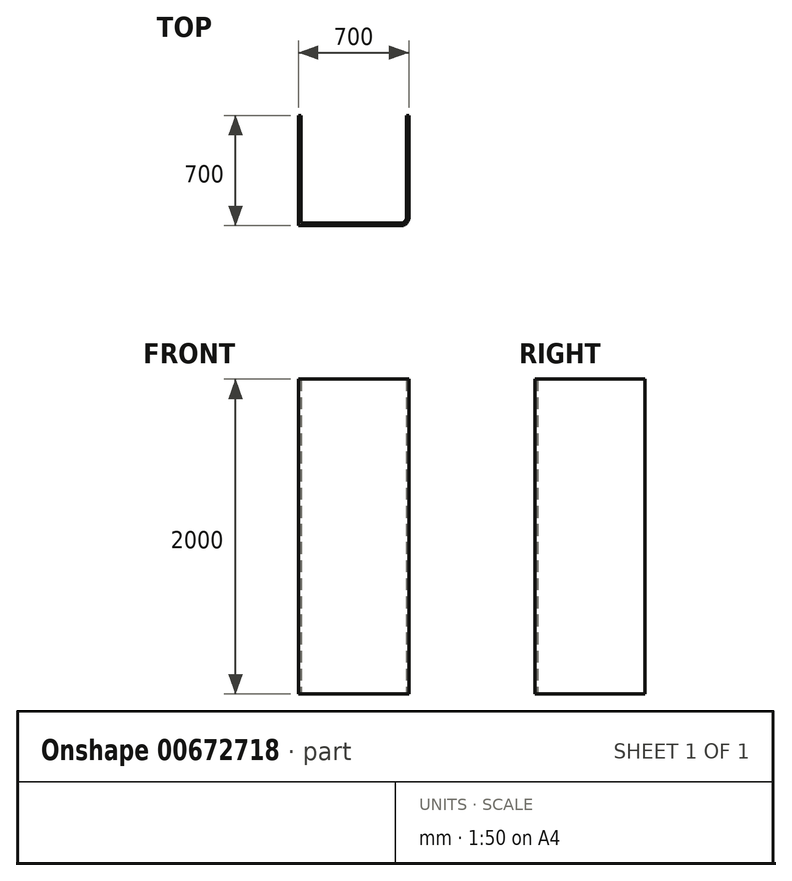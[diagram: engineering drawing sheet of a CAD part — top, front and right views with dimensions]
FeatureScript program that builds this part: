
annotation { "Feature Type Name" : "Feature", "Feature Type Description" : "" }
export const myFeature = defineFeature(function(context is Context, id is Id, definition is map)
    precondition{}
    {
        {
            var Q0;
            Q0=qCreatedBy(makeId("Top.planeOp"),FACE);
            var sketch = newSketch(context, id + "F0", { "sketchPlane" : qUnion([Q0])});
            skLineSegment(sketch, "E0.bottom", {"start": v(0, 0) * mm, "end": v(-700, 0) * mm});
            skLineSegment(sketch, "E0.top", {"start": v(0, -700) * mm, "end": v(-700, -700) * mm});
            skLineSegment(sketch, "E0.left", {"start": v(0, 0) * mm, "end": v(0, -700) * mm});
            skLineSegment(sketch, "E0.right", {"start": v(-700, 0) * mm, "end": v(-700, -700) * mm});
            skSolve(sketch);
        }
        {
            var Q0;
            Q0=makeQuery(id+"F0.imprint","IMPRINT",FACE,{"disambiguationData":[TD([[makeQuery(id+"F0.imprint","IMPRINT",EDGE,{"derivedFrom":sQuery(id+"F0.wireOp",EDGE,"Y66rWitT-qBWe-ztKi-yuPp-pPcdfemAuZkT.bottom")}),-1.0]])]});
            var Q1;
            Q1=makeQuery(id+"F0.imprint","IMPRINT",FACE,{"disambiguationData":[TD([[makeQuery(id+"F0.imprint","IMPRINT",EDGE,{"derivedFrom":sQuery(id+"F0.wireOp",EDGE,"E0.bottom")}),1.0]])]});
            extrude(context, id + "F1", {"entities" : qUnion([Q0, Q1]), "depth" : 2000 * mm, "offsetDistance" : 25 * mm});
        }
        {
            var Q0;
            Q0=makeQuery(id+"F1.opExtrude","SWEPT_FACE",FACE,{"disambiguationData":[OSD([sQuery(id+"F0.wireOp",EDGE,"E0.bottom")])]});
            var Q1;
            Q1=makeQuery(id+"F1.opExtrude","CAP_FACE",FACE,{"disambiguationData":[OSD([sQuery(id+"F0.wireOp",EDGE,"E0.bottom"),sQuery(id+"F0.wireOp",EDGE,"E0.top"),sQuery(id+"F0.wireOp",EDGE,"E0.left"),sQuery(id+"F0.wireOp",EDGE,"E0.right")])],"isStart":false});
            var Q2;
            Q2=makeQuery(id+"F1.opExtrude","CAP_FACE",FACE,{"disambiguationData":[OSD([sQuery(id+"F0.wireOp",EDGE,"E0.bottom"),sQuery(id+"F0.wireOp",EDGE,"E0.top"),sQuery(id+"F0.wireOp",EDGE,"E0.left"),sQuery(id+"F0.wireOp",EDGE,"E0.right")])],"isStart":true});
            shell(context, id + "F2", {"entities" : qUnion([Q0, Q1, Q2]), "thickness" : 16 * mm});
        }
        {
            var Q0;
            Q0=makeQuery(id+"F1.opExtrude","SWEPT_EDGE",EDGE,{"disambiguationData":[OSD([sQuery(id+"F0.wireOp",EDGE,"E0.top"),sQuery(id+"F0.wireOp",EDGE,"E0.left")])]});
            fillet(context, id + "F3", {"entities" : qUnion([Q0]), "radius" : 50 * mm, "tangentPropagation" : true, "allowEdgeOverflow" : false});
        }
        {
            var Q0;
            Q0=makeQuery(id+"F2.opShell","OFFSET_EDGE",EDGE,{"disambiguationData":[OSD([sQuery(id+"F0.wireOp",EDGE,"E0.top"),sQuery(id+"F0.wireOp",EDGE,"E0.left")])]});
            fillet(context, id + "F4", {"entities" : qUnion([Q0]), "radius" : 34 * mm, "tangentPropagation" : true, "allowEdgeOverflow" : false});
        }
    });
